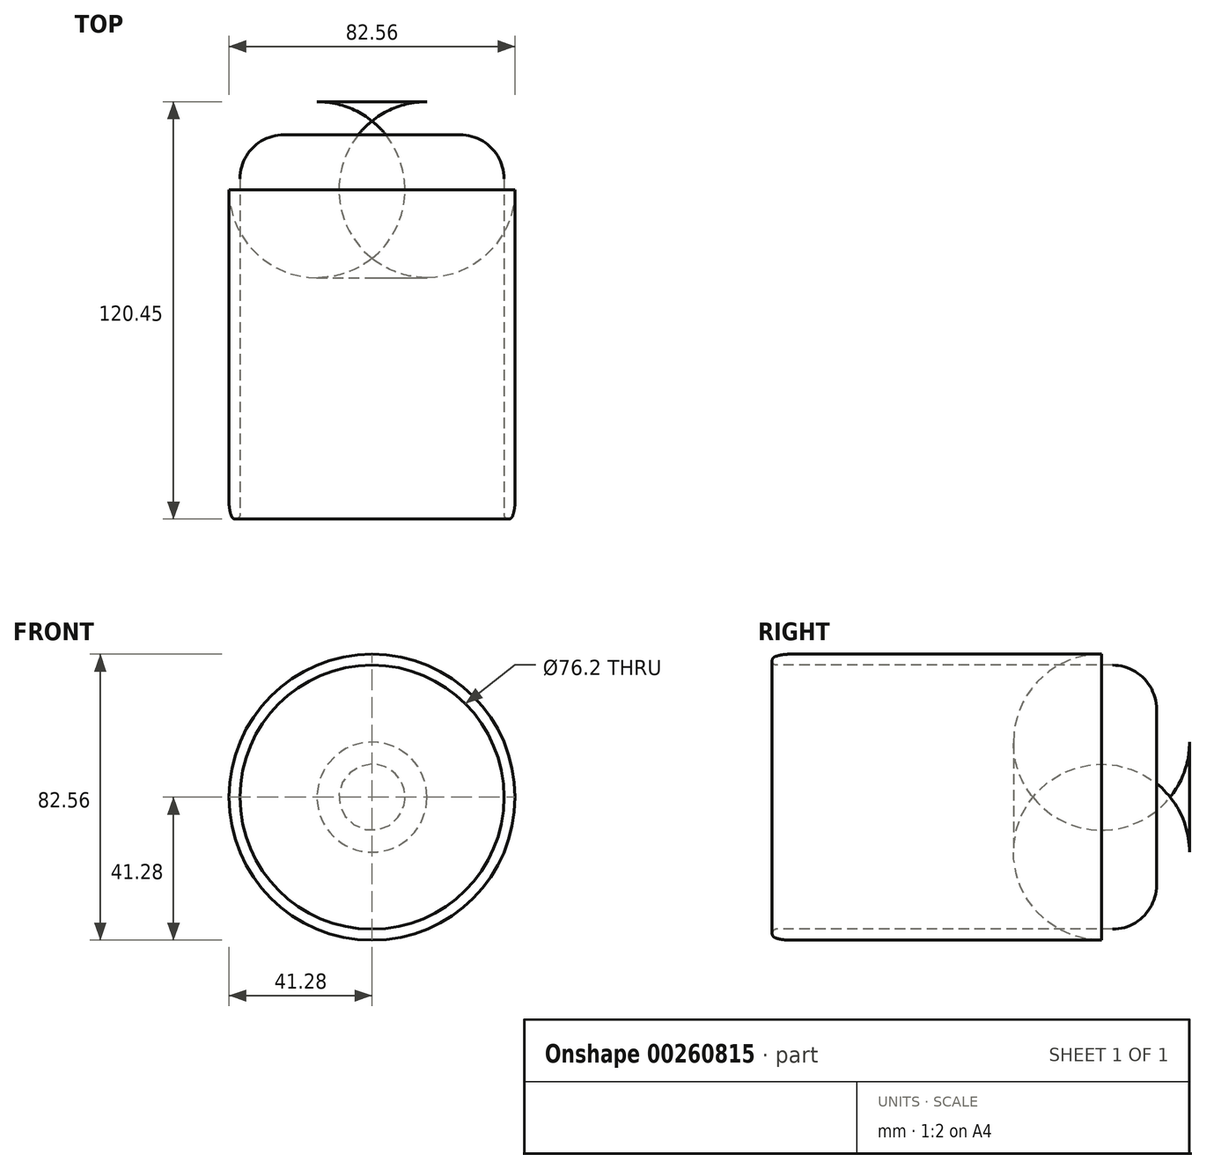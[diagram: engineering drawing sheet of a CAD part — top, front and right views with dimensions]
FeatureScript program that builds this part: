
annotation { "Feature Type Name" : "Feature", "Feature Type Description" : "" }
export const myFeature = defineFeature(function(context is Context, id is Id, definition is map)
    precondition{}
    {
        {
            var Q0;
            Q0=qCreatedBy(makeId("Front.planeOp"),FACE);
            var sketch = newSketch(context, id + "F0", { "sketchPlane" : qUnion([Q0])});
            skCircle(sketch, "E0", {"center": v(0, 0) * mm, "radius": 41.28 * mm});
            skSolve(sketch);
        }
        {
            var Q0;
            Q0=makeQuery(id+"F0.imprint","IMPRINT",FACE,{"disambiguationData":[TD([[makeQuery(id+"F0.imprint","IMPRINT",EDGE,{"derivedFrom":sQuery(id+"F0.wireOp",EDGE,"E0")}),1.0]])]});
            extrude(context, id + "F1", {"entities" : qUnion([Q0]), "depth" : 123.82 * mm});
        }
        {
            var Q0;
            Q0=makeQuery(id+"F1.opExtrude","CAP_FACE",FACE,{"disambiguationData":[OSD([sQuery(id+"F0.wireOp",EDGE,"E0")])],"isStart":false});
            var sketch = newSketch(context, id + "F2", { "sketchPlane" : qUnion([Q0])});
            skCircle(sketch, "E1", {"center": v(0, 0) * mm, "radius": 38.1 * mm});
            skSolve(sketch);
        }
        {
            var Q0;
            Q0=makeQuery(id+"F2.imprint","IMPRINT",FACE,{"disambiguationData":[TD([[makeQuery(id+"F2.imprint","IMPRINT",EDGE,{"derivedFrom":sQuery(id+"F2.wireOp",EDGE,"E1")}),1.0]])]});
            extrude(context, id + "F3", {"entities" : qUnion([Q0]), "operationType" : NewBodyOperationType.REMOVE, "oppositeDirection" : true, "depth" : 114.3 * mm});
        }
        {
            var Q0;
            Q0=makeQuery(id+"F1.opExtrude","CAP_EDGE",EDGE,{"disambiguationData":[OSD([sQuery(id+"F0.wireOp",EDGE,"E0")])],"isStart":false});
            var Q1;
            Q1=makeQuery(id+"F3.boolean.opBoolean","COPY",EDGE,{"derivedFrom":makeQuery(id+"F3.opExtrude","CAP_EDGE",EDGE,{"disambiguationData":[OSD([sQuery(id+"F2.wireOp",EDGE,"E1")])],"isStart":false})});
            fillet(context, id + "F4", {"entities" : qUnion([Q0, Q1]), "radius" : 12.7 * mm, "tangentPropagation" : true, "allowEdgeOverflow" : false});
        }
        {
            var Q0;
            Q0=makeQuery(id+"F4.opFillet","BLEND_EDGE",EDGE,{"blendedFrom":[makeQuery(id+"F1.opExtrude","CAP_EDGE",EDGE,{"disambiguationData":[OSD([sQuery(id+"F0.wireOp",EDGE,"E0")])],"isStart":false}),makeQuery(id+"F3.boolean.opBoolean","COPY",FACE,{"derivedFrom":makeQuery(id+"F3.opExtrude","SWEPT_FACE",FACE,{"disambiguationData":[OSD([sQuery(id+"F2.wireOp",EDGE,"E1")])]})})],"blendedInto":[makeQuery(id+"F3.boolean.opBoolean","COPY",FACE,{"derivedFrom":makeQuery(id+"F3.opExtrude","SWEPT_FACE",FACE,{"disambiguationData":[OSD([sQuery(id+"F2.wireOp",EDGE,"E1")])]})})]});
            fillet(context, id + "F5", {"entities" : qUnion([Q0]), "radius" : 1.27 * mm, "tangentPropagation" : true, "allowEdgeOverflow" : false});
        }
        {
            var Q0;
            Q0=makeQuery(id+"F1.opExtrude","CAP_EDGE",EDGE,{"disambiguationData":[OSD([sQuery(id+"F0.wireOp",EDGE,"E0")])],"isStart":true});
            fillet(context, id + "F6", {"entities" : qUnion([Q0]), "radius" : 25.4 * mm, "tangentPropagation" : true, "allowEdgeOverflow" : false});
        }
    });
